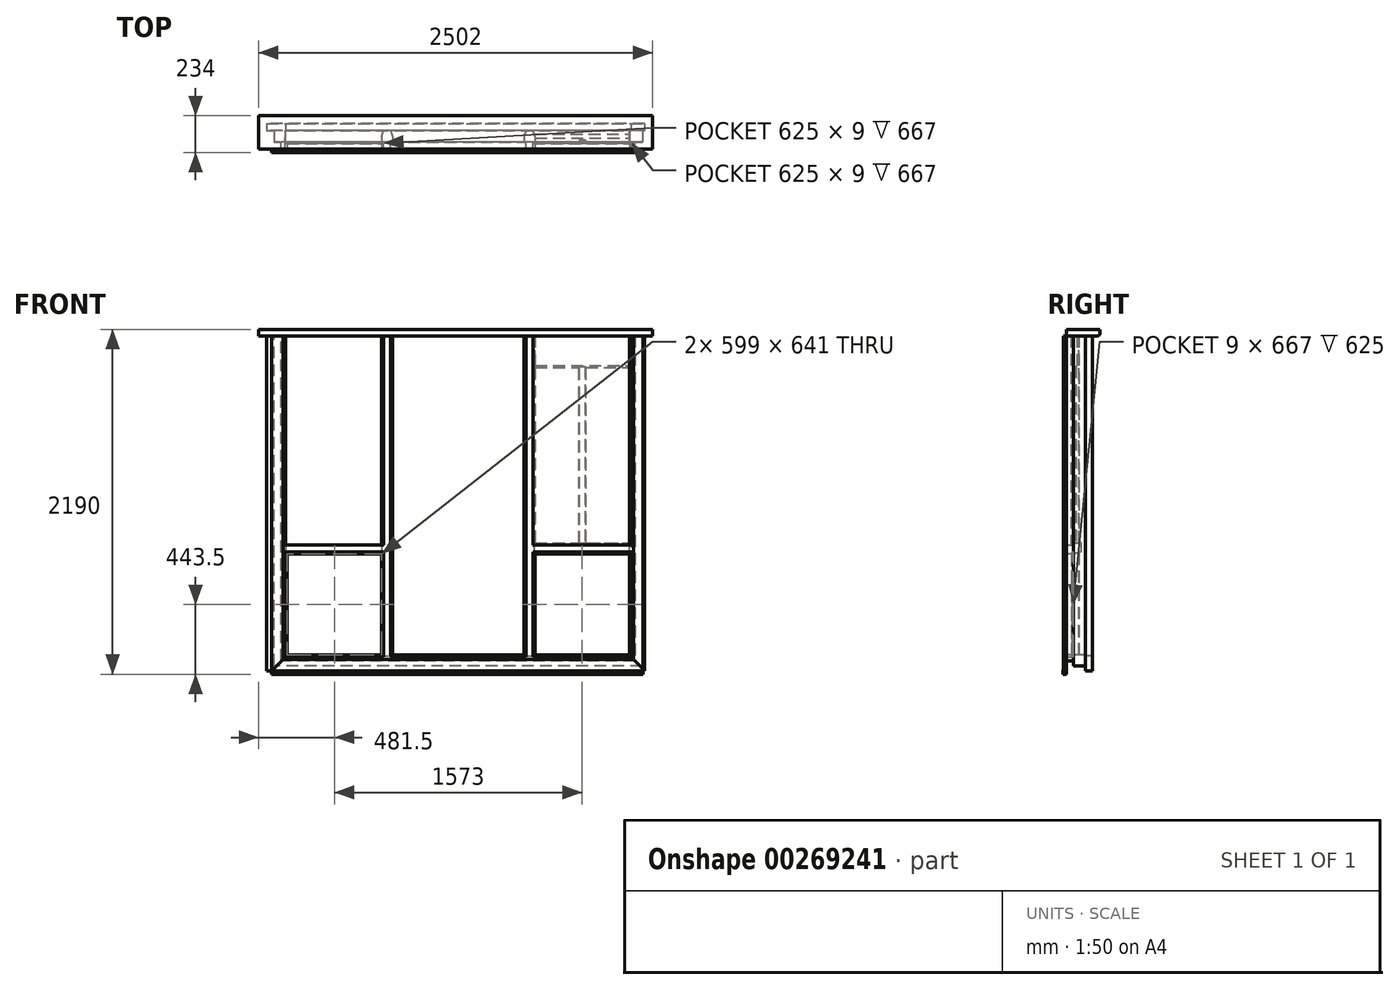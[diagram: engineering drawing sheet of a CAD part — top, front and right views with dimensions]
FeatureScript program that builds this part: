
annotation { "Feature Type Name" : "Feature", "Feature Type Description" : "" }
export const myFeature = defineFeature(function(context is Context, id is Id, definition is map)
    precondition{}
    {
        {
            var Q0;
            Q0=qCreatedBy(makeId("Front.planeOp"),FACE);
            var sketch = newSketch(context, id + "F0", { "sketchPlane" : qUnion([Q0])});
            skLineSegment(sketch, "E0", {"start": v(431, 0) * mm, "end": v(474, 0) * mm});
            skLineSegment(sketch, "E1", {"start": v(474, 0) * mm, "end": v(474, -1330) * mm});
            skLineSegment(sketch, "E2", {"start": v(474, -1330) * mm, "end": v(1099, -1330) * mm});
            skLineSegment(sketch, "E3", {"start": v(1099, -1330) * mm, "end": v(1099, 0) * mm});
            skLineSegment(sketch, "E4", {"start": v(1099, 0) * mm, "end": v(1124, 0) * mm});
            skLineSegment(sketch, "E5", {"start": v(1124, 0) * mm, "end": v(1124, -2065) * mm});
            skLineSegment(sketch, "E6", {"start": v(1124, -2065) * mm, "end": v(-1124, -2065) * mm});
            skLineSegment(sketch, "E7", {"start": v(-1124, -2065) * mm, "end": v(-1124, 0) * mm});
            skLineSegment(sketch, "E8", {"start": v(-1124, 0) * mm, "end": v(-1099, 0) * mm});
            skLineSegment(sketch, "E9", {"start": v(-1099, 0) * mm, "end": v(-1099, -1330) * mm});
            skLineSegment(sketch, "E10", {"start": v(-1099, -1330) * mm, "end": v(-474, -1330) * mm});
            skLineSegment(sketch, "E11", {"start": v(-474, -1330) * mm, "end": v(-474, 0) * mm});
            skLineSegment(sketch, "E12", {"start": v(-474, 0) * mm, "end": v(-431, 0) * mm});
            skLineSegment(sketch, "E13", {"start": v(-431, 0) * mm, "end": v(-431, -2040) * mm});
            skLineSegment(sketch, "E14", {"start": v(-431, -2040) * mm, "end": v(431, -2040) * mm});
            skLineSegment(sketch, "E15", {"start": v(431, -2040) * mm, "end": v(431, 0) * mm});
            skLineSegment(sketch, "E16", {"start": v(474, -2040) * mm, "end": v(1099, -2040) * mm});
            skLineSegment(sketch, "E17", {"start": v(1099, -2040) * mm, "end": v(1099, -1373) * mm});
            skLineSegment(sketch, "E18", {"start": v(1099, -1373) * mm, "end": v(474, -1373) * mm});
            skLineSegment(sketch, "E19", {"start": v(474, -1373) * mm, "end": v(474, -2040) * mm});
            skLineSegment(sketch, "E20", {"start": v(-474, -2040) * mm, "end": v(-1099, -2040) * mm});
            skLineSegment(sketch, "E21", {"start": v(-1099, -2040) * mm, "end": v(-1099, -1373) * mm});
            skLineSegment(sketch, "E22", {"start": v(-1099, -1373) * mm, "end": v(-474, -1373) * mm});
            skLineSegment(sketch, "E23", {"start": v(-474, -1373) * mm, "end": v(-474, -2040) * mm});
            skSolve(sketch);
        }
        {
            var Q0;
            Q0=makeQuery(id+"F0.imprint","IMPRINT",FACE,{"disambiguationData":[TD([[makeQuery(id+"F0.imprint","IMPRINT",EDGE,{"derivedFrom":sQuery(id+"F0.wireOp",EDGE,"E0")}),-1.0]])]});
            extrude(context, id + "F1", {"entities" : qUnion([Q0]), "depth" : 45 * mm});
        }
        {
            var Q0;
            Q0=makeQuery(id+"F1.opExtrude","CAP_FACE",FACE,{"disambiguationData":[OSD([sQuery(id+"F0.wireOp",EDGE,"E0"),sQuery(id+"F0.wireOp",EDGE,"E1"),sQuery(id+"F0.wireOp",EDGE,"E2"),sQuery(id+"F0.wireOp",EDGE,"E3"),sQuery(id+"F0.wireOp",EDGE,"E4"),sQuery(id+"F0.wireOp",EDGE,"E5"),sQuery(id+"F0.wireOp",EDGE,"E6"),sQuery(id+"F0.wireOp",EDGE,"E7"),sQuery(id+"F0.wireOp",EDGE,"E8"),sQuery(id+"F0.wireOp",EDGE,"E9"),sQuery(id+"F0.wireOp",EDGE,"E10"),sQuery(id+"F0.wireOp",EDGE,"E11"),sQuery(id+"F0.wireOp",EDGE,"E12"),sQuery(id+"F0.wireOp",EDGE,"E13"),sQuery(id+"F0.wireOp",EDGE,"E14"),sQuery(id+"F0.wireOp",EDGE,"E15"),sQuery(id+"F0.wireOp",EDGE,"E16"),sQuery(id+"F0.wireOp",EDGE,"E17"),sQuery(id+"F0.wireOp",EDGE,"E18"),sQuery(id+"F0.wireOp",EDGE,"E19"),sQuery(id+"F0.wireOp",EDGE,"E20"),sQuery(id+"F0.wireOp",EDGE,"E21"),sQuery(id+"F0.wireOp",EDGE,"E22"),sQuery(id+"F0.wireOp",EDGE,"E23")])],"isStart":false});
            cPlane(context, id + "F2", {"entities" : qUnion([Q0]), "cplaneType" : CPlaneType.OFFSET, "offset" : 2 * mm, "oppositeDirection" : true, "width" : 150 * mm, "height" : 150 * mm});
        }
        {
            var Q0;
            Q0=qCreatedBy(id+"F2.planeOp",FACE);
            var sketch = newSketch(context, id + "F3", { "sketchPlane" : qUnion([Q0])});
            skLineSegment(sketch, "E24.bottom", {"start": v(1086, -2027) * mm, "end": v(487, -2027) * mm});
            skLineSegment(sketch, "E24.top", {"start": v(1086, -1386) * mm, "end": v(487, -1386) * mm});
            skLineSegment(sketch, "E24.left", {"start": v(1086, -2027) * mm, "end": v(1086, -1386) * mm});
            skLineSegment(sketch, "E24.right", {"start": v(487, -2027) * mm, "end": v(487, -1386) * mm});
            skLineSegment(sketch, "E25.bottom", {"start": v(1109, -2050) * mm, "end": v(464, -2050) * mm});
            skLineSegment(sketch, "E25.top", {"start": v(1109, -1363) * mm, "end": v(464, -1363) * mm});
            skLineSegment(sketch, "E25.left", {"start": v(1109, -2050) * mm, "end": v(1109, -1363) * mm});
            skLineSegment(sketch, "E25.right", {"start": v(464, -2050) * mm, "end": v(464, -1363) * mm});
            skSolve(sketch);
        }
        {
            var Q0;
            Q0=makeQuery(id+"F3.imprint","IMPRINT",FACE,{"disambiguationData":[TD([[makeQuery(id+"F3.imprint","IMPRINT",EDGE,{"derivedFrom":sQuery(id+"F3.wireOp",EDGE,"E24.bottom")}),1.0]])]});
            extrude(context, id + "F4", {"entities" : qUnion([Q0]), "operationType" : NewBodyOperationType.ADD, "oppositeDirection" : true, "depth" : 34 * mm});
        }
        {
            var Q0;
            Q0=makeQuery(id+"F1.opExtrude","CAP_FACE",FACE,{"disambiguationData":[OSD([sQuery(id+"F0.wireOp",EDGE,"E0"),sQuery(id+"F0.wireOp",EDGE,"E1"),sQuery(id+"F0.wireOp",EDGE,"E2"),sQuery(id+"F0.wireOp",EDGE,"E3"),sQuery(id+"F0.wireOp",EDGE,"E4"),sQuery(id+"F0.wireOp",EDGE,"E5"),sQuery(id+"F0.wireOp",EDGE,"E6"),sQuery(id+"F0.wireOp",EDGE,"E7"),sQuery(id+"F0.wireOp",EDGE,"E8"),sQuery(id+"F0.wireOp",EDGE,"E9"),sQuery(id+"F0.wireOp",EDGE,"E10"),sQuery(id+"F0.wireOp",EDGE,"E11"),sQuery(id+"F0.wireOp",EDGE,"E12"),sQuery(id+"F0.wireOp",EDGE,"E13"),sQuery(id+"F0.wireOp",EDGE,"E14"),sQuery(id+"F0.wireOp",EDGE,"E15"),sQuery(id+"F0.wireOp",EDGE,"E16"),sQuery(id+"F0.wireOp",EDGE,"E17"),sQuery(id+"F0.wireOp",EDGE,"E18"),sQuery(id+"F0.wireOp",EDGE,"E19"),sQuery(id+"F0.wireOp",EDGE,"E20"),sQuery(id+"F0.wireOp",EDGE,"E21"),sQuery(id+"F0.wireOp",EDGE,"E22"),sQuery(id+"F0.wireOp",EDGE,"E23")])],"isStart":true});
            var sketch = newSketch(context, id + "F5", { "sketchPlane" : qUnion([Q0])});
            skLineSegment(sketch, "E26", {"start": v(-1099, -2027) * mm, "end": v(-488, -2027) * mm});
            skLineSegment(sketch, "E27", {"start": v(418, -2027) * mm, "end": v(418, 0) * mm});
            skLineSegment(sketch, "E28", {"start": v(418, 0) * mm, "end": v(488, 0) * mm});
            skPoint(sketch, "E28.endSnap0", {"position": v(452.5, 0) * mm});
            skLineSegment(sketch, "E29", {"start": v(488, 0) * mm, "end": v(488, -2027) * mm});
            skLineSegment(sketch, "E30", {"start": v(-418, -2027) * mm, "end": v(-418, 0) * mm});
            skLineSegment(sketch, "E31", {"start": v(-418, 0) * mm, "end": v(-488, 0) * mm});
            skPoint(sketch, "E31.endSnap0", {"position": v(-452.5, 0) * mm});
            skLineSegment(sketch, "E32", {"start": v(-488, 0) * mm, "end": v(-488, -2027) * mm});
            skLineSegment(sketch, "E33.trimOffspring", {"start": v(-418, -2027) * mm, "end": v(418, -2027) * mm});
            skLineSegment(sketch, "E34.trimOffspring", {"start": v(488, -2027) * mm, "end": v(1099, -2027) * mm});
            skLineSegment(sketch, "E35", {"start": v(-1099, -2027) * mm, "end": v(-1099, 0) * mm});
            skLineSegment(sketch, "E36", {"start": v(-1099, 0) * mm, "end": v(-1169, 0) * mm});
            skLineSegment(sketch, "E37", {"start": v(-1169, 0) * mm, "end": v(-1169, -2097) * mm});
            skLineSegment(sketch, "E38", {"start": v(-1169, -2097) * mm, "end": v(1169, -2097) * mm});
            skLineSegment(sketch, "E39", {"start": v(1169, -2097) * mm, "end": v(1169, 0) * mm});
            skLineSegment(sketch, "E40", {"start": v(1169, 0) * mm, "end": v(1099, 0) * mm});
            skLineSegment(sketch, "E41", {"start": v(1099, 0) * mm, "end": v(1099, -2027) * mm});
            skSolve(sketch);
        }
        {
            var Q0;
            Q0=makeQuery(id+"F1.opExtrude","SWEPT_BODY",BODY,{"disambiguationData":[OSD([sQuery(id+"F0.wireOp",EDGE,"E0"),sQuery(id+"F0.wireOp",EDGE,"E1"),sQuery(id+"F0.wireOp",EDGE,"E2"),sQuery(id+"F0.wireOp",EDGE,"E3"),sQuery(id+"F0.wireOp",EDGE,"E4"),sQuery(id+"F0.wireOp",EDGE,"E5"),sQuery(id+"F0.wireOp",EDGE,"E6"),sQuery(id+"F0.wireOp",EDGE,"E7"),sQuery(id+"F0.wireOp",EDGE,"E8"),sQuery(id+"F0.wireOp",EDGE,"E9"),sQuery(id+"F0.wireOp",EDGE,"E10"),sQuery(id+"F0.wireOp",EDGE,"E11"),sQuery(id+"F0.wireOp",EDGE,"E12"),sQuery(id+"F0.wireOp",EDGE,"E13"),sQuery(id+"F0.wireOp",EDGE,"E14"),sQuery(id+"F0.wireOp",EDGE,"E15"),sQuery(id+"F0.wireOp",EDGE,"E16"),sQuery(id+"F0.wireOp",EDGE,"E17"),sQuery(id+"F0.wireOp",EDGE,"E18"),sQuery(id+"F0.wireOp",EDGE,"E19"),sQuery(id+"F0.wireOp",EDGE,"E20"),sQuery(id+"F0.wireOp",EDGE,"E21"),sQuery(id+"F0.wireOp",EDGE,"E22"),sQuery(id+"F0.wireOp",EDGE,"E23")])]});
            var Q1;
            Q1=qCreatedBy(makeId("Right.planeOp"),FACE);
            mirror(context, id + "F6", {"operationType" : NewBodyOperationType.ADD, "entities" : qUnion([Q0]), "mirrorPlane" : qUnion([Q1])});
        }
        {
            var Q0;
            Q0 = qSketchRegion(id + "F5", true);
            extrude(context, id + "F7", {"entities" : qUnion([Q0]), "operationType" : NewBodyOperationType.ADD, "depth" : 75 * mm});
        }
        {
            var Q0;
            Q0=makeQuery(id+"F1.opExtrude","CAP_FACE",FACE,{"disambiguationData":[OSD([sQuery(id+"F0.wireOp",EDGE,"E0"),sQuery(id+"F0.wireOp",EDGE,"E1"),sQuery(id+"F0.wireOp",EDGE,"E2"),sQuery(id+"F0.wireOp",EDGE,"E3"),sQuery(id+"F0.wireOp",EDGE,"E4"),sQuery(id+"F0.wireOp",EDGE,"E5"),sQuery(id+"F0.wireOp",EDGE,"E6"),sQuery(id+"F0.wireOp",EDGE,"E7"),sQuery(id+"F0.wireOp",EDGE,"E8"),sQuery(id+"F0.wireOp",EDGE,"E9"),sQuery(id+"F0.wireOp",EDGE,"E10"),sQuery(id+"F0.wireOp",EDGE,"E11"),sQuery(id+"F0.wireOp",EDGE,"E12"),sQuery(id+"F0.wireOp",EDGE,"E13"),sQuery(id+"F0.wireOp",EDGE,"E14"),sQuery(id+"F0.wireOp",EDGE,"E15"),sQuery(id+"F0.wireOp",EDGE,"E16"),sQuery(id+"F0.wireOp",EDGE,"E17"),sQuery(id+"F0.wireOp",EDGE,"E18"),sQuery(id+"F0.wireOp",EDGE,"E19"),sQuery(id+"F0.wireOp",EDGE,"E20"),sQuery(id+"F0.wireOp",EDGE,"E21"),sQuery(id+"F0.wireOp",EDGE,"E22"),sQuery(id+"F0.wireOp",EDGE,"E23")])],"isStart":false});
            var sketch = newSketch(context, id + "F8", { "sketchPlane" : qUnion([Q0])});
            skLineSegment(sketch, "E42", {"start": v(1114, -2055) * mm, "end": v(-1114, -2055) * mm});
            skLineSegment(sketch, "E43", {"start": v(-1114, -2055) * mm, "end": v(-1114, 0) * mm});
            skLineSegment(sketch, "E44", {"start": v(-1114, 0) * mm, "end": v(-1187, 0) * mm});
            skLineSegment(sketch, "E45", {"start": v(-1187, 0) * mm, "end": v(-1187, -2150) * mm});
            skLineSegment(sketch, "E46", {"start": v(-1187, -2150) * mm, "end": v(1174, -2150) * mm});
            skLineSegment(sketch, "E47", {"start": v(1174, -2150) * mm, "end": v(1174, 0) * mm});
            skLineSegment(sketch, "E48", {"start": v(1174, 0) * mm, "end": v(1114, 0) * mm});
            skLineSegment(sketch, "E49", {"start": v(1114, 0) * mm, "end": v(1114, -2055) * mm});
            skSolve(sketch);
        }
        {
            var Q0;
            Q0 = qSketchRegion(id + "F8", true);
            extrude(context, id + "F9", {"entities" : qUnion([Q0]), "operationType" : NewBodyOperationType.ADD, "depth" : 20 * mm});
        }
        {
            var Q0;
            Q0=makeQuery(id+"F9.opExtrude","CAP_EDGE",EDGE,{"disambiguationData":[OSD([sQuery(id+"F8.wireOp",EDGE,"E42")])],"isStart":false});
            var Q1;
            Q1=makeQuery(id+"F9.opExtrude","CAP_EDGE",EDGE,{"disambiguationData":[OSD([sQuery(id+"F8.wireOp",EDGE,"E43")])],"isStart":false});
            var Q2;
            Q2=makeQuery(id+"F9.opExtrude","CAP_EDGE",EDGE,{"disambiguationData":[OSD([sQuery(id+"F8.wireOp",EDGE,"E49")])],"isStart":false});
            chamfer(context, id + "F10", {"entities" : qUnion([Q0, Q1, Q2]), "chamferType" : ChamferType.TWO_OFFSETS, "width1" : 12 * mm, "oppositeDirection" : true, "width2" : 75 * mm, "tangentPropagation" : true});
        }
        {
            var Q0;
            Q0=makeQuery(id+"F7.opExtrude","CAP_EDGE",EDGE,{"disambiguationData":[OSD([sQuery(id+"F5.wireOp",EDGE,"E29")])],"isStart":false});
            var Q1;
            Q1=makeQuery(id+"F7.opExtrude","CAP_EDGE",EDGE,{"disambiguationData":[OSD([sQuery(id+"F5.wireOp",EDGE,"E27")])],"isStart":false});
            var Q2;
            Q2=makeQuery(id+"F7.opExtrude","CAP_EDGE",EDGE,{"disambiguationData":[OSD([sQuery(id+"F5.wireOp",EDGE,"E32")])],"isStart":false});
            var Q3;
            Q3=makeQuery(id+"F7.opExtrude","CAP_EDGE",EDGE,{"disambiguationData":[OSD([sQuery(id+"F5.wireOp",EDGE,"E30")])],"isStart":false});
            chamfer(context, id + "F11", {"entities" : qUnion([Q0, Q1, Q2, Q3]), "chamferType" : ChamferType.TWO_OFFSETS, "width1" : 12.5 * mm, "oppositeDirection" : true, "width2" : 40 * mm, "tangentPropagation" : true});
        }
        {
            var Q0;
            {var subQ1=sQuery(id+"F0.wireOp",EDGE,"E17");var subQ3=sQuery(id+"F0.wireOp",EDGE,"E3");Q0=makeQuery(id+"F7.boolean.opBoolean","MERGE",FACE,{"derivedFrom":[makeQuery(id+"F1.opExtrude","SWEPT_FACE",FACE,{"disambiguationData":[OSD([subQ3])]}),makeQuery(id+"F4.boolean.opBoolean","SPLIT",FACE,{"disambiguationData":[TD([makeQuery(id+"F4.opExtrude","CAP_FACE",FACE,{"disambiguationData":[OSD([sQuery(id+"F3.wireOp",EDGE,"E24.bottom"),sQuery(id+"F3.wireOp",EDGE,"E24.top"),sQuery(id+"F3.wireOp",EDGE,"E24.left"),sQuery(id+"F3.wireOp",EDGE,"E24.right"),sQuery(id+"F3.wireOp",EDGE,"E25.bottom"),sQuery(id+"F3.wireOp",EDGE,"E25.top"),sQuery(id+"F3.wireOp",EDGE,"E25.left"),sQuery(id+"F3.wireOp",EDGE,"E25.right")])],"isStart":false})])],"derivedFrom":makeQuery(id+"F1.opExtrude","SWEPT_FACE",FACE,{"disambiguationData":[OSD([subQ1])]})}),makeQuery(id+"F7.opExtrude","SWEPT_FACE",FACE,{"disambiguationData":[OSD([sQuery(id+"F5.wireOp",EDGE,"E35")])]})]});}
            var sketch = newSketch(context, id + "F12", { "sketchPlane" : qUnion([Q0])});
            skLineSegment(sketch, "E50", {"start": v(0, -1373) * mm, "end": v(0, -2027) * mm});
            skLineSegment(sketch, "E51", {"start": v(0, -2027) * mm, "end": v(-75, -2027) * mm});
            skLineSegment(sketch, "E52", {"start": v(-75, -2027) * mm, "end": v(-75, 0) * mm});
            skLineSegment(sketch, "E53", {"start": v(-75, 0) * mm, "end": v(15, 0) * mm});
            skLineSegment(sketch, "E54", {"start": v(15, 0) * mm, "end": v(15, -1330) * mm});
            skLineSegment(sketch, "E55", {"start": v(15, -1330) * mm, "end": v(0, -1330) * mm});
            skLineSegment(sketch, "E56", {"start": v(0, -1330) * mm, "end": v(0, -1373) * mm});
            skSolve(sketch);
        }
        {
            var Q0;
            Q0 = qSketchRegion(id + "F12", true);
            extrude(context, id + "F13", {"entities" : qUnion([Q0]), "operationType" : NewBodyOperationType.ADD, "depth" : 10 * mm});
        }
        {
            var Q0;
            Q0=makeQuery(id+"F13.opExtrude","CAP_FACE",FACE,{"disambiguationData":[OSD([sQuery(id+"F12.wireOp",EDGE,"E50"),sQuery(id+"F12.wireOp",EDGE,"E51"),sQuery(id+"F12.wireOp",EDGE,"E52"),sQuery(id+"F12.wireOp",EDGE,"E53"),sQuery(id+"F12.wireOp",EDGE,"E54"),sQuery(id+"F12.wireOp",EDGE,"E55"),sQuery(id+"F12.wireOp",EDGE,"E56")])],"isStart":false});
            var sketch = newSketch(context, id + "F14", { "sketchPlane" : qUnion([Q0])});
            skLineSegment(sketch, "E57", {"start": v(0, -1373) * mm, "end": v(0, -1386) * mm});
            skLineSegment(sketch, "E58", {"start": v(0, -1386) * mm, "end": v(-50, -1371) * mm});
            skLineSegment(sketch, "E59", {"start": v(-50, -1371) * mm, "end": v(-50, -1316) * mm});
            skLineSegment(sketch, "E60", {"start": v(-50, -1316) * mm, "end": v(0, -1316) * mm});
            skLineSegment(sketch, "E61", {"start": v(0, -1316) * mm, "end": v(0, -200) * mm});
            skLineSegment(sketch, "E62", {"start": v(0, -200) * mm, "end": v(-25, -190) * mm});
            skLineSegment(sketch, "E63", {"start": v(-25, -190) * mm, "end": v(-25, 0) * mm});
            skLineSegment(sketch, "E64", {"start": v(-25, 0) * mm, "end": v(5, 0) * mm});
            skLineSegment(sketch, "E65", {"start": v(5, 0) * mm, "end": v(5, -1330) * mm});
            skLineSegment(sketch, "E66", {"start": v(5, -1330) * mm, "end": v(0, -1330) * mm});
            skLineSegment(sketch, "E67", {"start": v(0, -1330) * mm, "end": v(0, -1373) * mm});
            skSolve(sketch);
        }
        {
            var Q0;
            Q0 = qSketchRegion(id + "F14", true);
            extrude(context, id + "F15", {"entities" : qUnion([Q0]), "operationType" : NewBodyOperationType.ADD, "depth" : 620 * mm});
        }
        {
            var Q0;
            Q0=makeQuery(id+"F15.opExtrude","SWEPT_FACE",FACE,{"disambiguationData":[OSD([sQuery(id+"F14.wireOp",EDGE,"E61")])]});
            var sketch = newSketch(context, id + "F16", { "sketchPlane" : qUnion([Q0])});
            skLineSegment(sketch, "E68.bottom", {"start": v(-766, -1316) * mm, "end": v(-811, -1316) * mm});
            skLineSegment(sketch, "E68.top", {"start": v(-766, -190) * mm, "end": v(-811, -190) * mm});
            skLineSegment(sketch, "E68.left", {"start": v(-766, -1316) * mm, "end": v(-766, -190) * mm});
            skLineSegment(sketch, "E68.right", {"start": v(-811, -1316) * mm, "end": v(-811, -190) * mm});
            skSolve(sketch);
        }
        {
            var Q0;
            Q0 = qSketchRegion(id + "F16", true);
            extrude(context, id + "F17", {"entities" : qUnion([Q0]), "operationType" : NewBodyOperationType.ADD, "depth" : 15 * mm});
        }
        {
            var Q0;
            Q0=makeQuery(id+"F17.opExtrude","CAP_EDGE",EDGE,{"disambiguationData":[OSD([sQuery(id+"F16.wireOp",EDGE,"E68.left")])],"isStart":false});
            var Q1;
            Q1=makeQuery(id+"F17.opExtrude","CAP_EDGE",EDGE,{"disambiguationData":[OSD([sQuery(id+"F16.wireOp",EDGE,"E68.right")])],"isStart":false});
            chamfer(context, id + "F18", {"entities" : qUnion([Q0, Q1]), "chamferType" : ChamferType.TWO_OFFSETS, "width1" : 5 * mm, "oppositeDirection" : false, "width2" : 15 * mm, "tangentPropagation" : true});
        }
        {
            var Q0;
            Q0=makeQuery(id+"F7.opExtrude","CAP_FACE",FACE,{"disambiguationData":[OSD([sQuery(id+"F5.wireOp",EDGE,"E26"),sQuery(id+"F5.wireOp",EDGE,"E27"),sQuery(id+"F5.wireOp",EDGE,"E28"),sQuery(id+"F5.wireOp",EDGE,"E29"),sQuery(id+"F5.wireOp",EDGE,"E30"),sQuery(id+"F5.wireOp",EDGE,"E31"),sQuery(id+"F5.wireOp",EDGE,"E32"),sQuery(id+"F5.wireOp",EDGE,"E33.trimOffspring"),sQuery(id+"F5.wireOp",EDGE,"E34.trimOffspring"),sQuery(id+"F5.wireOp",EDGE,"E35"),sQuery(id+"F5.wireOp",EDGE,"E36"),sQuery(id+"F5.wireOp",EDGE,"E37"),sQuery(id+"F5.wireOp",EDGE,"E38"),sQuery(id+"F5.wireOp",EDGE,"E39"),sQuery(id+"F5.wireOp",EDGE,"E40"),sQuery(id+"F5.wireOp",EDGE,"E41")])],"isStart":false});
            var sketch = newSketch(context, id + "F19", { "sketchPlane" : qUnion([Q0])});
            skLineSegment(sketch, "E69", {"start": v(1096, -2034) * mm, "end": v(-1096, -2034) * mm});
            skLineSegment(sketch, "E70", {"start": v(-1096, 0) * mm, "end": v(-1184, 0) * mm});
            skPoint(sketch, "E70.endSnap0", {"position": v(-1129, 0) * mm});
            skLineSegment(sketch, "E71", {"start": v(-1184, 0) * mm, "end": v(-1184, -2130) * mm});
            skLineSegment(sketch, "E72", {"start": v(-1184, -2130) * mm, "end": v(1218, -2130) * mm});
            skLineSegment(sketch, "E73", {"start": v(1218, -2130) * mm, "end": v(1218, 0) * mm});
            skLineSegment(sketch, "E74", {"start": v(1218, 0) * mm, "end": v(1096, 0) * mm});
            skLineSegment(sketch, "E75", {"start": v(1096, 0) * mm, "end": v(1096, -2034) * mm});
            skLineSegment(sketch, "E76", {"start": v(-1096, -2034) * mm, "end": v(-1096, 0) * mm});
            skSolve(sketch);
        }
        {
            var Q0;
            Q0 = qSketchRegion(id + "F19", true);
            extrude(context, id + "F20", {"entities" : qUnion([Q0]), "operationType" : NewBodyOperationType.ADD, "depth" : 44 * mm});
        }
        {
            var Q0;
            Q0=makeQuery(id+"F20.boolean.opBoolean","MERGE",FACE,{"derivedFrom":[makeQuery(id+"F15.boolean.opBoolean","MERGE",FACE,{"derivedFrom":[makeQuery(id+"F7.boolean.opBoolean","MERGE",FACE,{"derivedFrom":[makeQuery(id+"F1.opExtrude","SWEPT_FACE",FACE,{"disambiguationData":[OSD([sQuery(id+"F0.wireOp",EDGE,"E0")])]}),makeQuery(id+"F7.opExtrude","SWEPT_FACE",FACE,{"disambiguationData":[OSD([sQuery(id+"F5.wireOp",EDGE,"E31")])]})]}),makeQuery(id+"F13.boolean.opBoolean","MERGE",FACE,{"derivedFrom":[makeQuery(id+"F9.boolean.opBoolean","MERGE",FACE,{"derivedFrom":[makeQuery(id+"F7.boolean.opBoolean","MERGE",FACE,{"derivedFrom":[makeQuery(id+"F1.opExtrude","SWEPT_FACE",FACE,{"disambiguationData":[OSD([sQuery(id+"F0.wireOp",EDGE,"E4")])]}),makeQuery(id+"F7.opExtrude","SWEPT_FACE",FACE,{"disambiguationData":[OSD([sQuery(id+"F5.wireOp",EDGE,"E36")])]})]}),makeQuery(id+"F9.opExtrude","SWEPT_FACE",FACE,{"disambiguationData":[OSD([sQuery(id+"F8.wireOp",EDGE,"E48")])]})]}),makeQuery(id+"F13.opExtrude","SWEPT_FACE",FACE,{"disambiguationData":[OSD([sQuery(id+"F12.wireOp",EDGE,"E53")])]})]}),makeQuery(id+"F15.opExtrude","SWEPT_FACE",FACE,{"disambiguationData":[OSD([sQuery(id+"F14.wireOp",EDGE,"E64")])]})]}),makeQuery(id+"F20.opExtrude","SWEPT_FACE",FACE,{"disambiguationData":[OSD([sQuery(id+"F19.wireOp",EDGE,"E70")])]})]});
            var sketch = newSketch(context, id + "F21", { "sketchPlane" : qUnion([Q0])});
            skLineSegment(sketch, "E77", {"start": v(1124, -45) * mm, "end": v(1234, -45) * mm});
            skPoint(sketch, "E77.endSnap0", {"position": v(1149, -45) * mm});
            skLineSegment(sketch, "E78", {"start": v(1234, -45) * mm, "end": v(1234, 169) * mm});
            skLineSegment(sketch, "E79", {"start": v(1234, 169) * mm, "end": v(-1268, 169) * mm});
            skLineSegment(sketch, "E80", {"start": v(-1268, 169) * mm, "end": v(-1268, -45) * mm});
            skLineSegment(sketch, "E81", {"start": v(-1268, -45) * mm, "end": v(1124, -45) * mm});
            skSolve(sketch);
        }
        {
            var Q0;
            Q0 = qSketchRegion(id + "F21", true);
            extrude(context, id + "F22", {"entities" : qUnion([Q0]), "depth" : 40 * mm});
        }
        {
            var Q0;
            Q0=makeQuery(id+"F22.opExtrude","CAP_EDGE",EDGE,{"disambiguationData":[OSD([sQuery(id+"F21.wireOp",EDGE,"E79")])],"isStart":true});
            fillet(context, id + "F23", {"entities" : qUnion([Q0]), "radius" : 15 * mm, "tangentPropagation" : true, "allowEdgeOverflow" : false});
        }
    });
